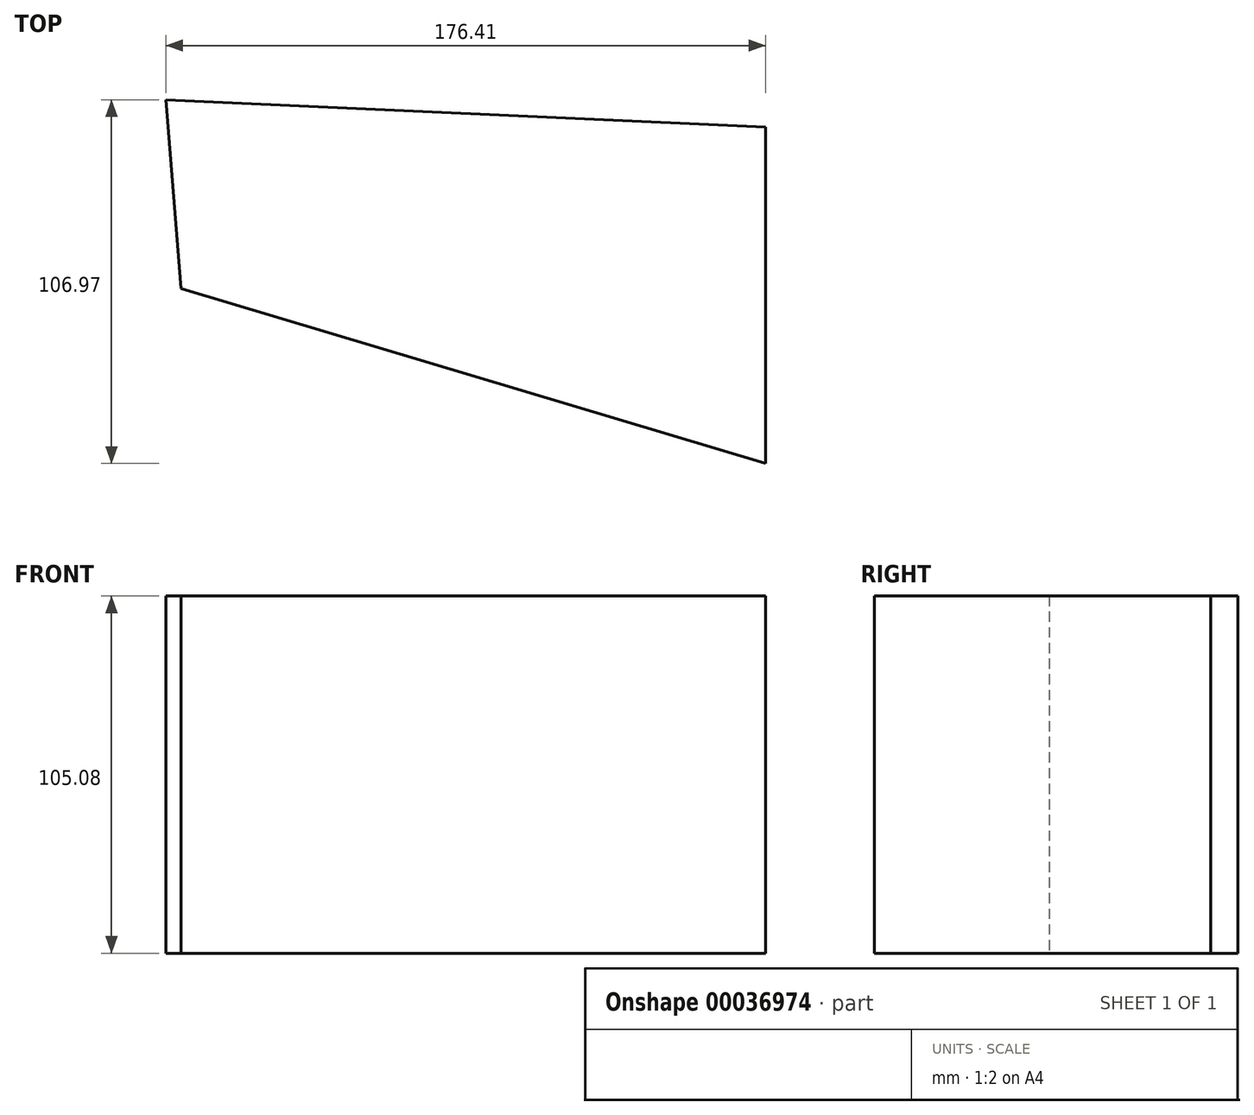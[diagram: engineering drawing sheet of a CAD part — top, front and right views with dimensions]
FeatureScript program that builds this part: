
annotation { "Feature Type Name" : "Feature", "Feature Type Description" : "" }
export const myFeature = defineFeature(function(context is Context, id is Id, definition is map)
    precondition{}
    {
        {
            var Q0;
            Q0=qCreatedBy(makeId("Top.planeOp"),FACE);
            var sketch = newSketch(context, id + "F0", { "sketchPlane" : qUnion([Q0])});
            skLineSegment(sketch, "E0", {"start": v(-112.97, 0) * mm, "end": v(-117.4, 55.49) * mm});
            skLineSegment(sketch, "E1", {"start": v(-117.4, 55.49) * mm, "end": v(59, 47.52) * mm});
            skLineSegment(sketch, "E2", {"start": v(59, 47.52) * mm, "end": v(59, -51.48) * mm});
            skLineSegment(sketch, "E3", {"start": v(-112.97, 0) * mm, "end": v(59, -51.48) * mm});
            skSolve(sketch);
        }
        {
            var Q0;
            Q0 = qSketchRegion(id + "FBsoOOldIPr5HGG_0", true);
            var Q1;
            Q1=makeQuery(id+"F0.imprint","IMPRINT",FACE,{"disambiguationData":[TD([[makeQuery(id+"F0.imprint","IMPRINT",EDGE,{"derivedFrom":sQuery(id+"F0.wireOp",EDGE,"E0")}),-1.0]])]});
            extrude(context, id + "F1", {"entities" : qUnion([Q0, Q1]), "endBound" : BoundingType.SYMMETRIC, "depth" : 105.07 * mm});
        }
    });
